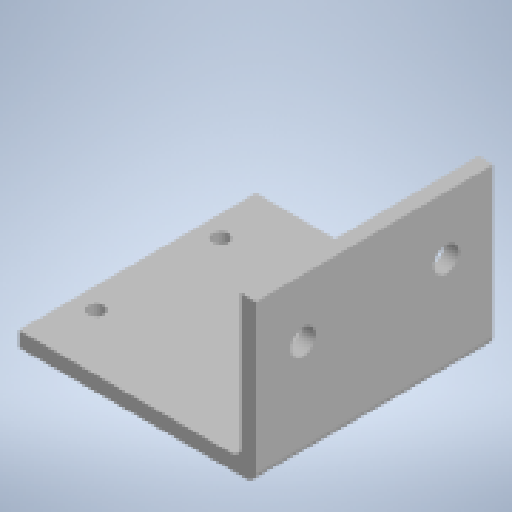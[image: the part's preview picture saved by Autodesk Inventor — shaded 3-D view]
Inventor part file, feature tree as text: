
AUTODESK INVENTOR PART (.ipt)
format: ipt  version: 2023 (Build 270158000, 158)  size: 170,496 bytes
history: native  units: in
note: dims shown in document units (in); Inventor stores cm internally (conversion verified against a paired STEP export)
features: extrude x3, sketch x3, shell x1, fillet x1, projected_geometry x1
ambient origin geometry x8: Origin, YZ Plane, XZ Plane, XY Plane, X Axis, Y Axis, Z Axis, Center Point
bodies: Solid1 (feature_tree)
feature tree (9):
  extrude  "Extrusion1"  Depth=2.0in
  shell  "Shell1"  Thickness=3.0in
  extrude  "Extrusion2"  Depth=0.125in
  extrude  "Extrusion3"  Depth=3.0in
  fillet  "Fillet1"  Radius=0.1969in
  sketch  "Sketch1"  dims[d0=3.0in d1=2.0in d2=3.0in d3=0.0in]
  sketch  "Sketch3"  dims[d4=0.1875in d5=0.125in]
  sketch  "Sketch4"  dims[d6=1.5748in d7=2.0866in d8=0.1969in d9=3.0in d10=0.0in d11=1.811in d12=0.315in d13=3.0in d14=0.0in d15=1.2598in d16=0.0in]
  projected_geometry  "Projected Loop1"
